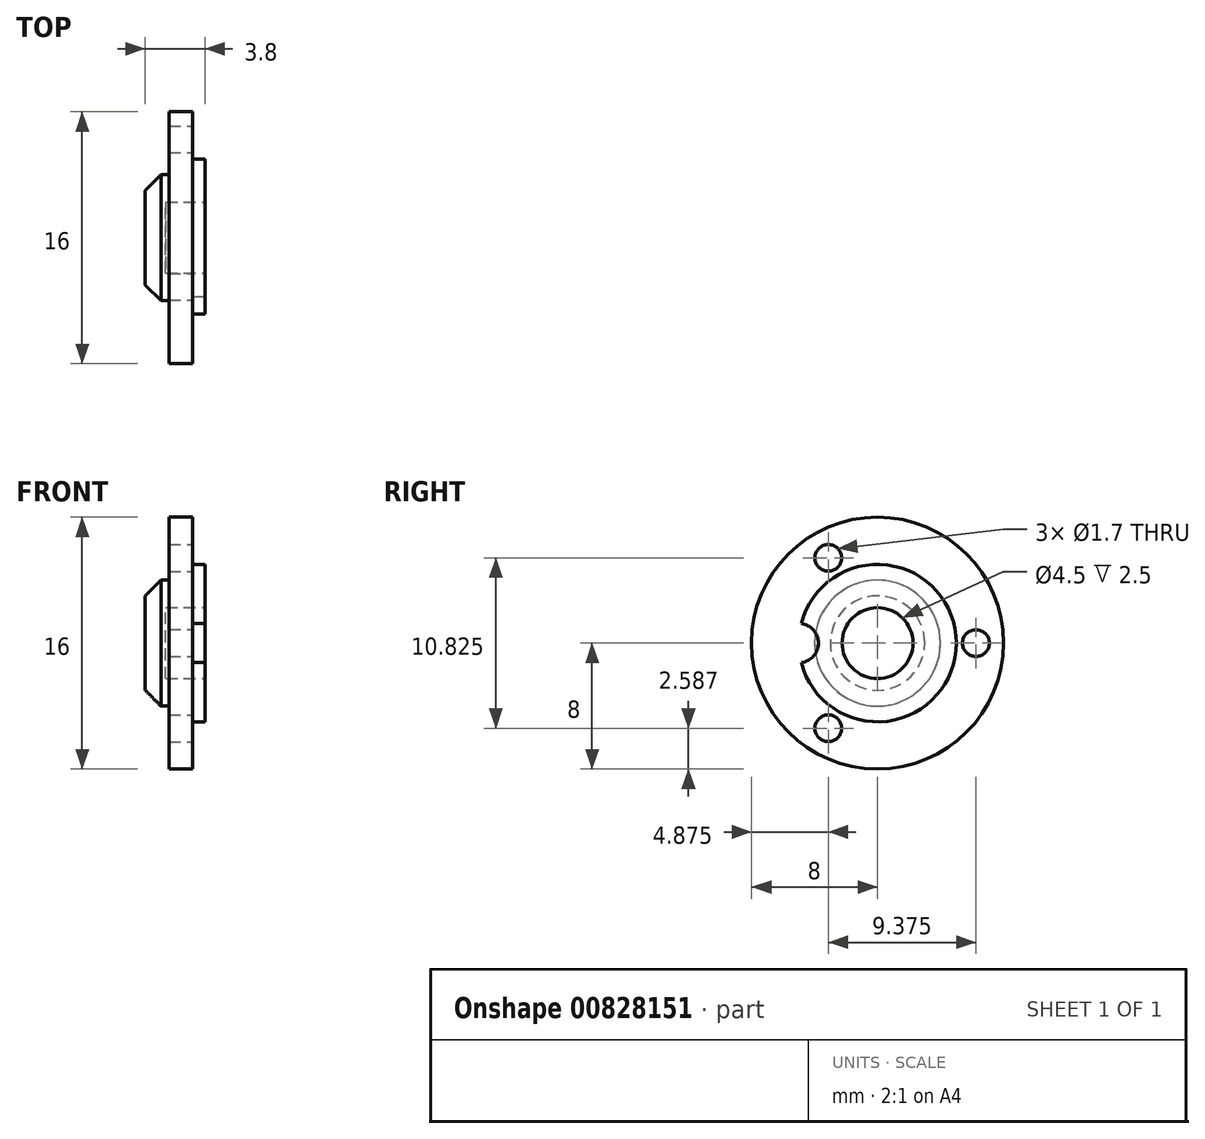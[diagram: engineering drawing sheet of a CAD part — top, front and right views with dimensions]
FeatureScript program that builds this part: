
annotation { "Feature Type Name" : "Feature", "Feature Type Description" : "" }
export const myFeature = defineFeature(function(context is Context, id is Id, definition is map)
    precondition{}
    {
        {
            var Q0;
            Q0=qCreatedBy(makeId("Front.planeOp"),FACE);
            var sketch = newSketch(context, id + "F0", { "sketchPlane" : qUnion([Q0])});
            skLineSegment(sketch, "E0", {"start": v(0, 0) * mm, "end": v(3.8, 0) * mm});
            skLineSegment(sketch, "E1", {"start": v(3.8, 0) * mm, "end": v(3.8, 5) * mm});
            skLineSegment(sketch, "E2", {"start": v(3.8, 5) * mm, "end": v(3, 5) * mm});
            skLineSegment(sketch, "E3", {"start": v(3, 5) * mm, "end": v(3, 8) * mm});
            skLineSegment(sketch, "E4", {"start": v(3, 8) * mm, "end": v(1.5, 8) * mm});
            skLineSegment(sketch, "E5", {"start": v(1.5, 8) * mm, "end": v(1.5, 4) * mm});
            skLineSegment(sketch, "E6", {"start": v(1.5, 4) * mm, "end": v(0, 4) * mm});
            skLineSegment(sketch, "E7", {"start": v(0, 4) * mm, "end": v(0, 0) * mm});
            skSolve(sketch);
        }
        {
            var Q0;
            Q0 = qSketchRegion(id + "F0", true);
            var Q1;
            Q1=sQuery(id+"F0.wireOp",EDGE,"E0");
            revolve(context, id + "F1", {"surfaceOperationType" : NewSurfaceOperationType.NEW, "entities" : qUnion([Q0]), "axis" : qUnion([Q1]), "revolveType" : RevolveType.FULL});
        }
        {
            var Q0;
            Q0=makeQuery(id+"F1.opRevolve","SWEPT_EDGE",EDGE,{"disambiguationData":[OSD([sQuery(id+"F0.wireOp",EDGE,"E6"),sQuery(id+"F0.wireOp",EDGE,"E7")])]});
            chamfer(context, id + "F2", {"entities" : qUnion([Q0]), "width" : 1 * mm, "tangentPropagation" : true});
        }
        {
            var Q0;
            Q0=makeQuery(id+"F1.opRevolve","SWEPT_FACE",FACE,{"disambiguationData":[OSD([sQuery(id+"F0.wireOp",EDGE,"E3")])]});
            var sketch = newSketch(context, id + "F3", { "sketchPlane" : qUnion([Q0])});
            skCircle(sketch, "E8", {"center": v(6.25, 0) * mm, "radius": 0.85 * mm});
            skCircle(sketch, "E9", {"center": v(-3.13, 5.41) * mm, "radius": 0.85 * mm});
            skCircle(sketch, "E10", {"center": v(-3.12, -5.41) * mm, "radius": 0.85 * mm});
            skCircle(sketch, "E11", {"center": v(0, 0) * mm, "radius": 6.25 * mm, "construction": true});
            skLineSegment(sketch, "E12", {"start": v(0, 0) * mm, "end": v(6.25, 0) * mm, "construction": true});
            skLineSegment(sketch, "E13", {"start": v(0, 0) * mm, "end": v(-3.12, -5.41) * mm, "construction": true});
            skLineSegment(sketch, "E14", {"start": v(0, 0) * mm, "end": v(-3.13, 5.41) * mm, "construction": true});
            skSolve(sketch);
        }
        {
            var Q0;
            Q0 = qSketchRegion(id + "F3", true);
            extrude(context, id + "F4", {"entities" : qUnion([Q0]), "operationType" : NewBodyOperationType.REMOVE, "endBound" : BoundingType.THROUGH_ALL, "oppositeDirection" : true, "depth" : 25 * mm, "offsetDistance" : 25 * mm});
        }
        {
            var Q0;
            Q0=makeQuery(id+"F1.opRevolve","SWEPT_FACE",FACE,{"disambiguationData":[OSD([sQuery(id+"F0.wireOp",EDGE,"E1")])]});
            var sketch = newSketch(context, id + "F5", { "sketchPlane" : qUnion([Q0])});
            skCircle(sketch, "E15", {"center": v(-5, 0) * mm, "radius": 1.25 * mm});
            skSolve(sketch);
        }
        {
            var Q0;
            Q0 = qSketchRegion(id + "F5", true);
            var Q1;
            Q1=makeQuery(id+"F1.opRevolve","SWEPT_FACE",FACE,{"disambiguationData":[OSD([sQuery(id+"F0.wireOp",EDGE,"E3")])]});
            extrude(context, id + "F6", {"entities" : qUnion([Q0]), "operationType" : NewBodyOperationType.REMOVE, "endBound" : BoundingType.UP_TO_SURFACE, "oppositeDirection" : true, "depth" : 25 * mm, "endBoundEntityFace" : qUnion([Q1]), "offsetDistance" : 25 * mm});
        }
        {
            var Q0;
            Q0=makeQuery(id+"F1.opRevolve","SWEPT_FACE",FACE,{"disambiguationData":[OSD([sQuery(id+"F0.wireOp",EDGE,"E1")])]});
            var sketch = newSketch(context, id + "F7", { "sketchPlane" : qUnion([Q0])});
            skCircle(sketch, "E16", {"center": v(0, 0) * mm, "radius": 2.25 * mm});
            skSolve(sketch);
        }
        {
            var Q0;
            Q0 = qSketchRegion(id + "F7", true);
            extrude(context, id + "F8", {"entities" : qUnion([Q0]), "operationType" : NewBodyOperationType.REMOVE, "oppositeDirection" : true, "depth" : 2.5 * mm, "offsetDistance" : 25 * mm});
        }
    });
